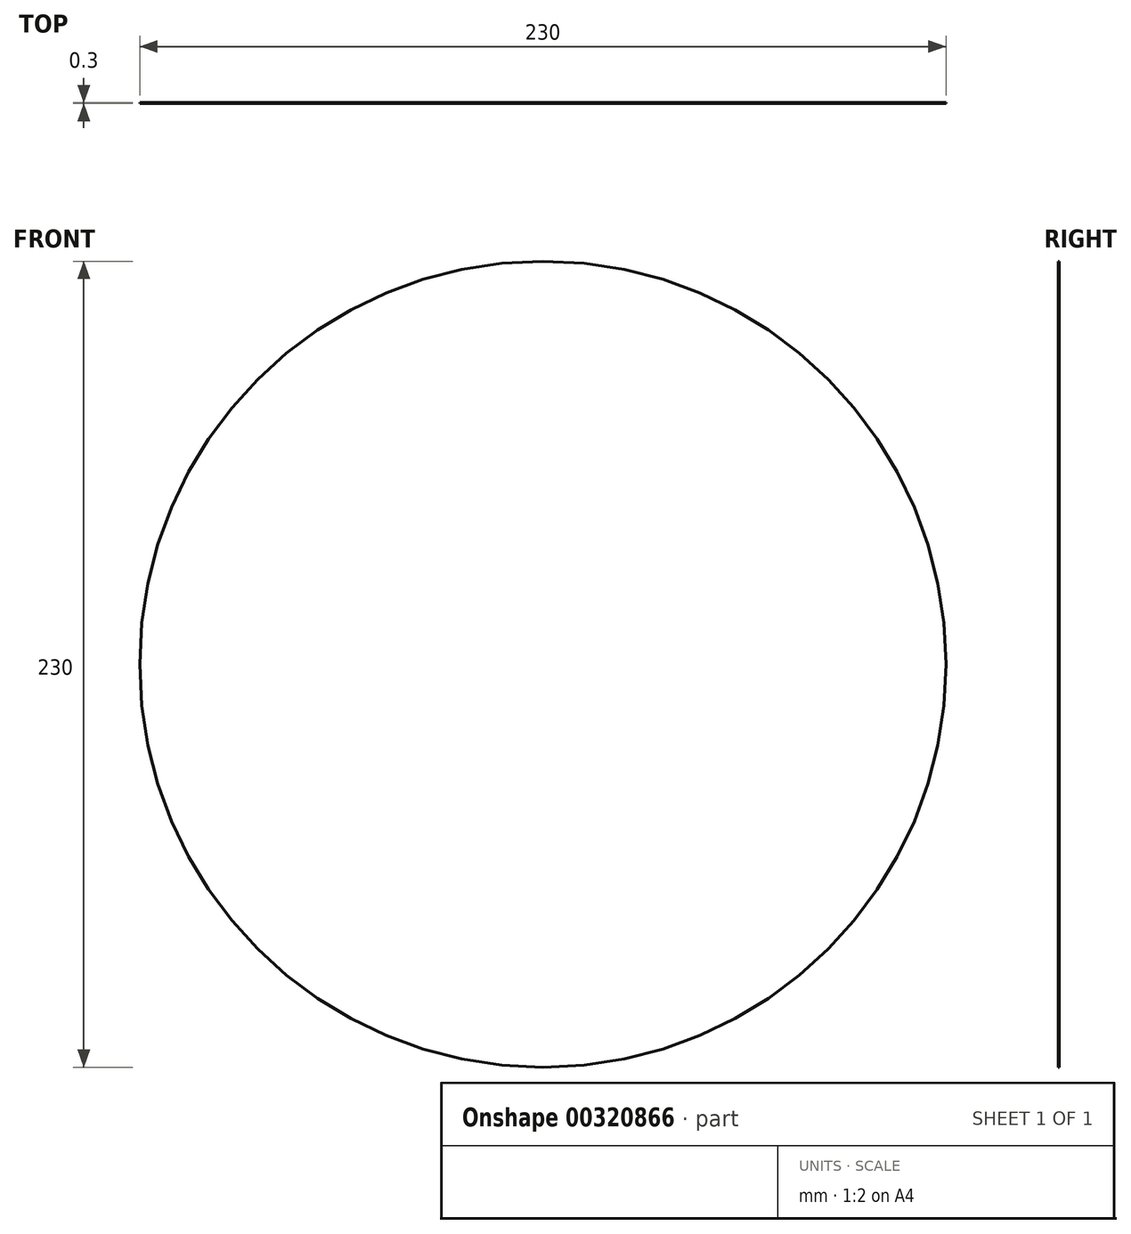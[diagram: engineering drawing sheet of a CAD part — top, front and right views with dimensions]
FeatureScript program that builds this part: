
annotation { "Feature Type Name" : "Feature", "Feature Type Description" : "" }
export const myFeature = defineFeature(function(context is Context, id is Id, definition is map)
    precondition{}
    {
        {
            var Q0;
            Q0=qCreatedBy(makeId("Front.planeOp"),FACE);
            var sketch = newSketch(context, id + "F0", { "sketchPlane" : qUnion([Q0])});
            skCircle(sketch, "E0.cCircle", {"center": v(16.82, -30.95) * mm, "radius": 129.9 * mm, "construction": true});
            skLineSegment(sketch, "E0.0", {"start": v(166.82, -30.95) * mm, "end": v(91.82, -160.85) * mm});
            skLineSegment(sketch, "E0.1", {"start": v(91.82, -160.85) * mm, "end": v(-58.18, -160.85) * mm});
            skLineSegment(sketch, "E0.2", {"start": v(-58.18, -160.85) * mm, "end": v(-133.18, -30.95) * mm});
            skLineSegment(sketch, "E0.3", {"start": v(-133.18, -30.95) * mm, "end": v(-58.18, 98.96) * mm});
            skLineSegment(sketch, "E0.4", {"start": v(-58.18, 98.96) * mm, "end": v(91.82, 98.96) * mm});
            skLineSegment(sketch, "E0.5", {"start": v(91.82, 98.96) * mm, "end": v(166.82, -30.95) * mm});
            skPoint(sketch, "E0.0.midPoint", {"position": v(129.32, -95.9) * mm});
            skCircle(sketch, "E1", {"center": v(16.82, -30.95) * mm, "radius": 115 * mm});
            skLineSegment(sketch, "E2.bottom", {"start": v(166.82, 98.96) * mm, "end": v(-133.18, 98.96) * mm});
            skLineSegment(sketch, "E2.top", {"start": v(166.82, -160.85) * mm, "end": v(-133.18, -160.85) * mm});
            skLineSegment(sketch, "E2.left", {"start": v(166.82, 98.96) * mm, "end": v(166.82, -160.85) * mm});
            skLineSegment(sketch, "E2.right", {"start": v(-133.18, 98.96) * mm, "end": v(-133.18, -160.85) * mm});
            skSolve(sketch);
        }
        {
            var Q0;
            Q0=makeQuery(id+"F0.imprint","IMPRINT",FACE,{"disambiguationData":[TD([[makeQuery(id+"F0.imprint","IMPRINT",EDGE,{"derivedFrom":sQuery(id+"F0.wireOp",EDGE,"E1")}),1.0]])]});
            extrude(context, id + "F1", {"entities" : qUnion([Q0]), "depth" : 0.3 * mm, "offsetDistance" : 25 * mm});
        }
    });
